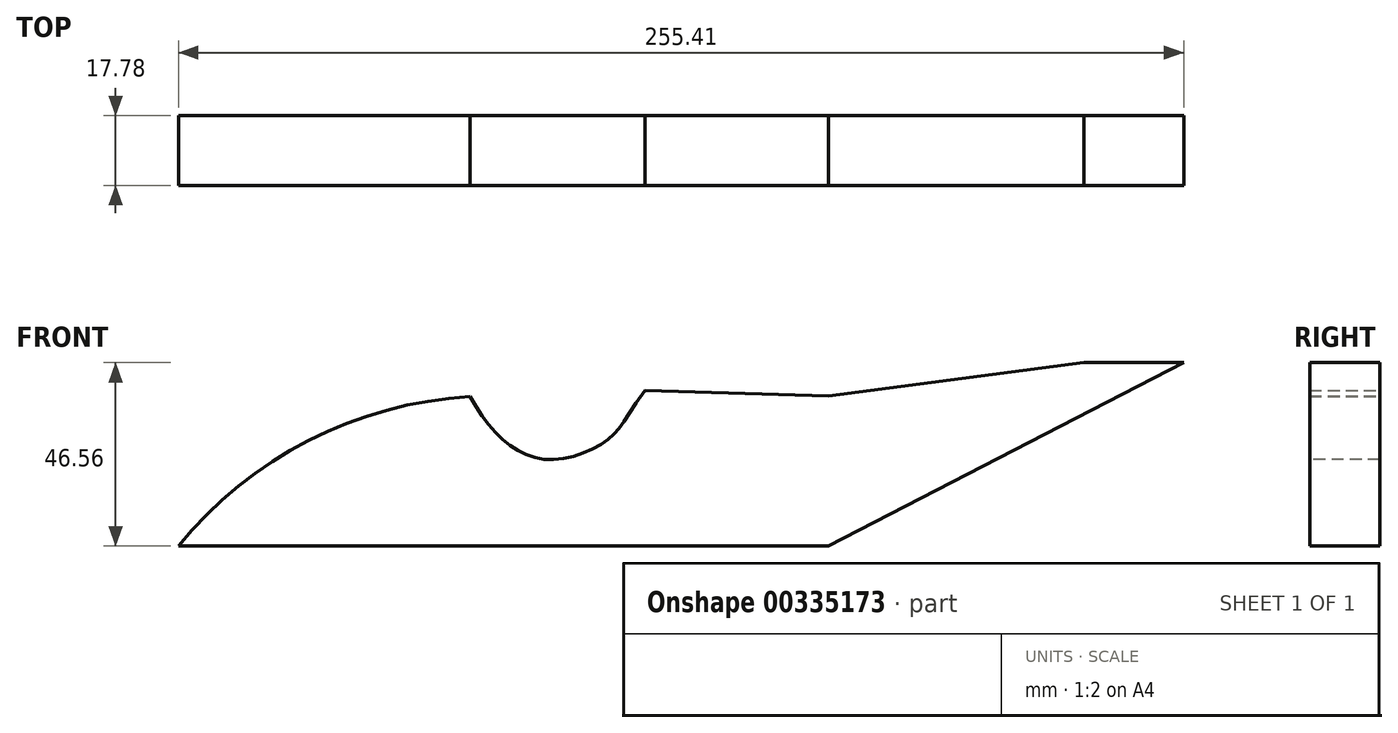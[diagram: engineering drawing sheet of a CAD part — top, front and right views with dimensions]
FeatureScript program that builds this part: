
annotation { "Feature Type Name" : "Feature", "Feature Type Description" : "" }
export const myFeature = defineFeature(function(context is Context, id is Id, definition is map)
    precondition{}
    {
        {
            var Q0;
            Q0=qCreatedBy(makeId("Front.planeOp"),FACE);
            var sketch = newSketch(context, id + "F0", { "sketchPlane" : qUnion([Q0])});
            skLineSegment(sketch, "E0", {"start": v(-162.1, -39.45) * mm, "end": v(3, -39.45) * mm});
            skLineSegment(sketch, "E1", {"start": v(3, -39.45) * mm, "end": v(93.31, 7.1) * mm});
            skLineSegment(sketch, "E2", {"start": v(93.31, 7.1) * mm, "end": v(67.91, 7.1) * mm});
            skLineSegment(sketch, "E3", {"start": v(-162.1, -39.45) * mm, "end": v(-162.1, -1.35) * mm});
            skLineSegment(sketch, "E4", {"start": v(3, -1.35) * mm, "end": v(67.91, 7.1) * mm});
            skLineSegment(sketch, "E5", {"start": v(-162.1, -1.35) * mm, "end": v(-88.07, -1.35) * mm});
            skLineSegment(sketch, "E6", {"start": v(3, -1.35) * mm, "end": v(-43.62, 0) * mm});
            skFitSpline(sketch, "E7", {"points": [v(-88.07, -1.35) * mm, v(-77.76, -14) * mm, v(-65.86, -17.46) * mm, v(-52.81, -12.28) * mm, v(-43.62, 0) * mm], "startDerivative": vector(32.6, -59.95) * mm, "endDerivative": vector(57.96, 80.55) * mm});
            skSolve(sketch);
        }
        {
            var Q0;
            Q0=makeQuery(id+"F0.imprint","IMPRINT",FACE,{"disambiguationData":[TD([[makeQuery(id+"F0.imprint","IMPRINT",EDGE,{"derivedFrom":sQuery(id+"F0.wireOp",EDGE,"E0")}),1.0]])]});
            extrude(context, id + "F1", {"entities" : qUnion([Q0]), "depth" : 17.78 * mm});
        }
        {
            var Q0;
            Q0=makeQuery(id+"F1.opExtrude","SWEPT_EDGE",EDGE,{"disambiguationData":[OSD([sQuery(id+"F0.wireOp",EDGE,"E3"),sQuery(id+"F0.wireOp",EDGE,"E5")])]});
            fillet(context, id + "F2", {"entities" : qUnion([Q0]), "radius" : 103.02 * mm, "tangentPropagation" : true, "allowEdgeOverflow" : false});
        }
    });
